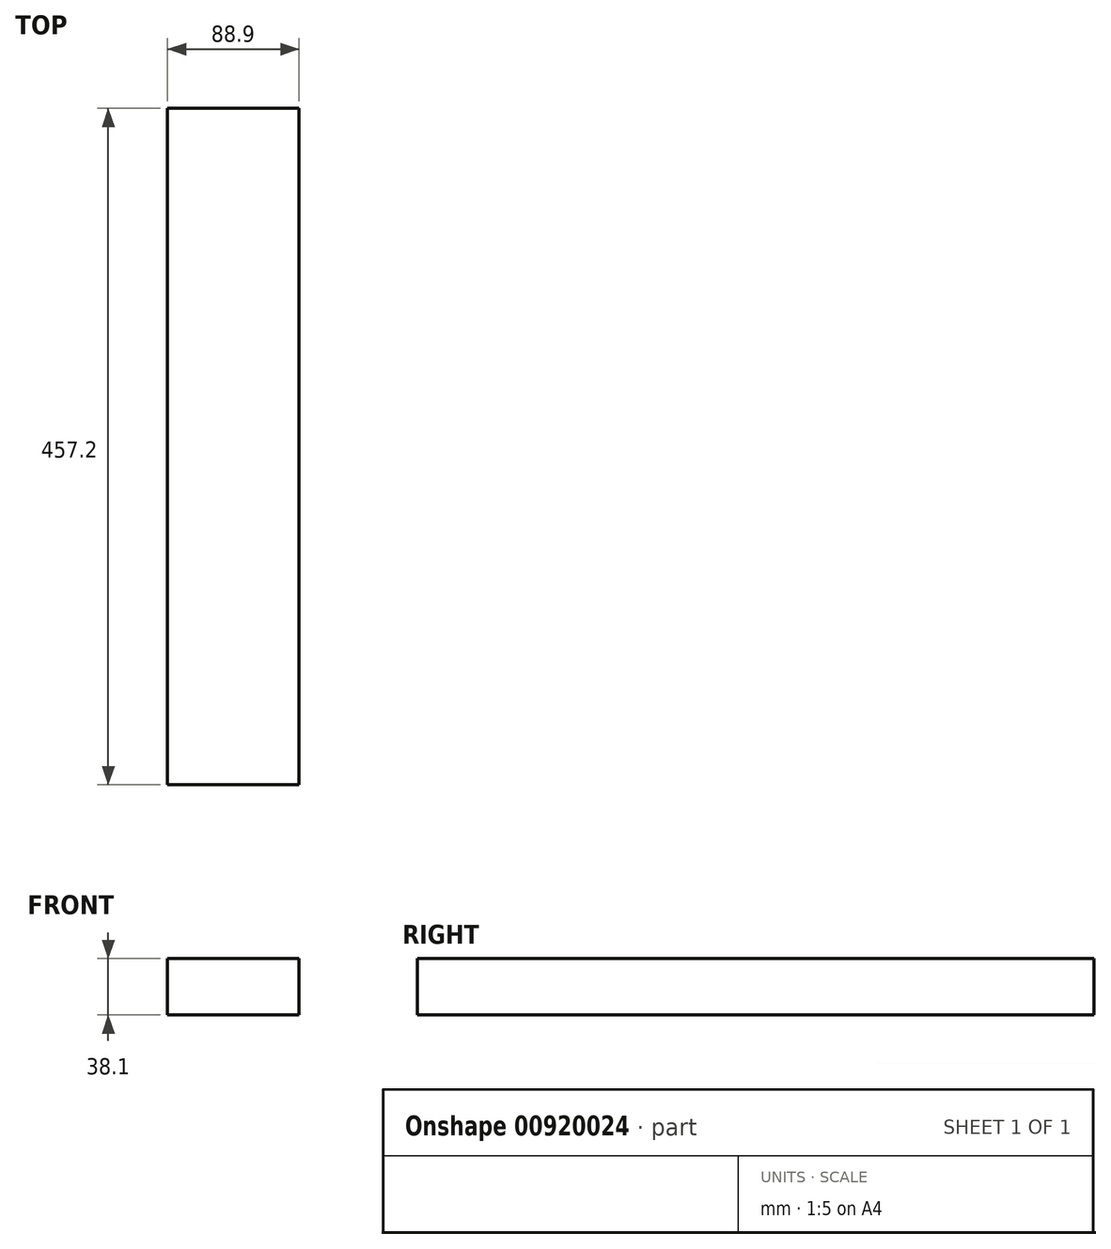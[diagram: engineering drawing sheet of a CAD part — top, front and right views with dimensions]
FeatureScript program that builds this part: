
annotation { "Feature Type Name" : "Feature", "Feature Type Description" : "" }
export const myFeature = defineFeature(function(context is Context, id is Id, definition is map)
    precondition{}
    {
        {
            var Q0;
            Q0=qCreatedBy(makeId("Front.planeOp"),FACE);
            var sketch = newSketch(context, id + "F0", { "sketchPlane" : qUnion([Q0])});
            skLineSegment(sketch, "E0.bottom", {"start": v(44.45, 19.05) * mm, "end": v(-44.45, 19.05) * mm});
            skLineSegment(sketch, "E0.top", {"start": v(44.45, -19.05) * mm, "end": v(-44.45, -19.05) * mm});
            skLineSegment(sketch, "E0.left", {"start": v(44.45, 19.05) * mm, "end": v(44.45, -19.05) * mm});
            skLineSegment(sketch, "E0.right", {"start": v(-44.45, 19.05) * mm, "end": v(-44.45, -19.05) * mm});
            skPoint(sketch, "E0.middle", {"position": v(0, 0) * mm});
            skSolve(sketch);
        }
        {
            var Q0;
            Q0 = qSketchRegion(id + "F0", true);
            extrude(context, id + "F1", {"entities" : qUnion([Q0]), "oppositeDirection" : true, "depth" : 457.2 * mm, "offsetDistance" : 25.4 * mm});
        }
    });
